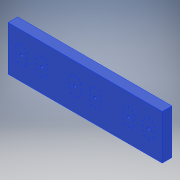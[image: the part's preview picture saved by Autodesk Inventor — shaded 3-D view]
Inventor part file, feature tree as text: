
AUTODESK INVENTOR PART (.ipt)
format: ipt  version: 2019 (Build 230136000, 136)  size: 404,480 bytes
history: native  units: mm
features: reference x92, other x9, extrude x7, sketch x7
ambient origin geometry x8: Origin, YZ Plane, XZ Plane, XY Plane, X Axis, Y Axis, Z Axis, Center Point
bodies: Body1 (feature_tree)
feature tree (115):
  extrude  "Extrusion2"  Depth=4.0mm TaperAngle=0.0deg
  extrude  "Extrusion3"  Depth=4.0mm TaperAngle=0.0deg
  extrude  "Extrusion4"  Depth=4.0mm TaperAngle=0.0deg
  extrude  "Extrusion5"  Depth=4.0mm TaperAngle=0.0deg
  extrude  "Extrusion6"  [1 undecoded]
  extrude  "Extrusion7"  [1 undecoded]
  extrude  "Extrusion8"  [1 undecoded]
  sketch  "Skizze1"  dims[d0=46.0mm d3=4.0mm d4=0.0mm]
  reference  "Referenz1"
  reference  "Referenz2"
  reference  "Referenz3"
  reference  "Referenz4"
  reference  "Referenz5"
  reference  "Referenz6"
  reference  "Referenz7"
  reference  "Referenz8"
  sketch  "Skizze2"  dims[d5=4.0mm d6=0.0mm d7=4.0mm d8=0.0mm]
  reference  "Referenz9"
  reference  "Referenz10"
  reference  "Referenz11"
  reference  "Referenz12"
  reference  "Referenz13"
  reference  "Referenz14"
  reference  "Referenz15"
  reference  "Referenz16"
  reference  "Referenz17"
  reference  "Referenz18"
  reference  "Referenz19"
  reference  "Referenz20"
  sketch  "Skizze3"  dims[d9=0.0mm d10=0.0mm d11=4.0mm d12=0.0mm]
  reference  "Referenz21"
  reference  "Referenz22"
  reference  "Referenz23"
  reference  "Referenz24"
  reference  "Referenz25"
  reference  "Referenz26"
  reference  "Referenz27"
  reference  "Referenz28"
  reference  "Referenz29"
  reference  "Referenz30"
  reference  "Referenz31"
  reference  "Referenz32"
  sketch  "Skizze4"  dims[d13=4.0mm d14=0.0mm d15=4.0mm d16=0.0mm]
  reference  "Referenz33"
  reference  "Referenz34"
  reference  "Referenz35"
  reference  "Referenz36"
  reference  "Referenz37"
  reference  "Referenz38"
  reference  "Referenz39"
  reference  "Referenz40"
  reference  "Referenz41"
  reference  "Referenz42"
  reference  "Referenz43"
  reference  "Referenz44"
  reference  "Referenz45"
  reference  "Referenz46"
  reference  "Referenz47"
  reference  "Referenz48"
  reference  "Referenz49"
  reference  "Referenz50"
  reference  "Referenz51"
  reference  "Referenz52"
  reference  "Referenz53"
  reference  "Referenz54"
  reference  "Referenz55"
  reference  "Referenz56"
  sketch  "Skizze5"
  reference  "Referenz57"
  reference  "Referenz58"
  reference  "Referenz59"
  reference  "Referenz60"
  reference  "Referenz61"
  reference  "Referenz62"
  reference  "Referenz63"
  reference  "Referenz64"
  reference  "Referenz65"
  reference  "Referenz66"
  reference  "Referenz67"
  reference  "Referenz68"
  sketch  "Skizze6"
  reference  "Referenz69"
  reference  "Referenz70"
  reference  "Referenz71"
  reference  "Referenz72"
  reference  "Referenz73"
  reference  "Referenz74"
  reference  "Referenz75"
  reference  "Referenz76"
  reference  "Referenz77"
  reference  "Referenz78"
  reference  "Referenz79"
  reference  "Referenz80"
  sketch  "Skizze7"
  reference  "Referenz81"
  reference  "Referenz82"
  reference  "Referenz83"
  reference  "Referenz84"
  reference  "Referenz85"
  reference  "Referenz86"
  reference  "Referenz87"
  reference  "Referenz88"
  reference  "Referenz89"
  reference  "Referenz90"
  reference  "Referenz91"
  reference  "Referenz92"
  parser-record x1  (decoder bookkeeping rows leaked as tree rows — omitted from the tree; the rows remain in map.json)
  other  "Zusammenbau.iam"
  other  "IN-12a:1"
  other  "IN-12a:2"
  other  "IN-12a:3"
  other  "IN-12a:4"
  other  "IN-12a:5"
  other  "IN-12a:6"
  other  "NixieModule_IN12.brd:2"
note: 3 required parameter values undecoded (feature->parameter linkage not recoverable at this tier; creation-order binding heuristic only, values carry confidence <= 0.55)
note: 1 file-system path scrubbed to <path> (originals preserved in map.json)
